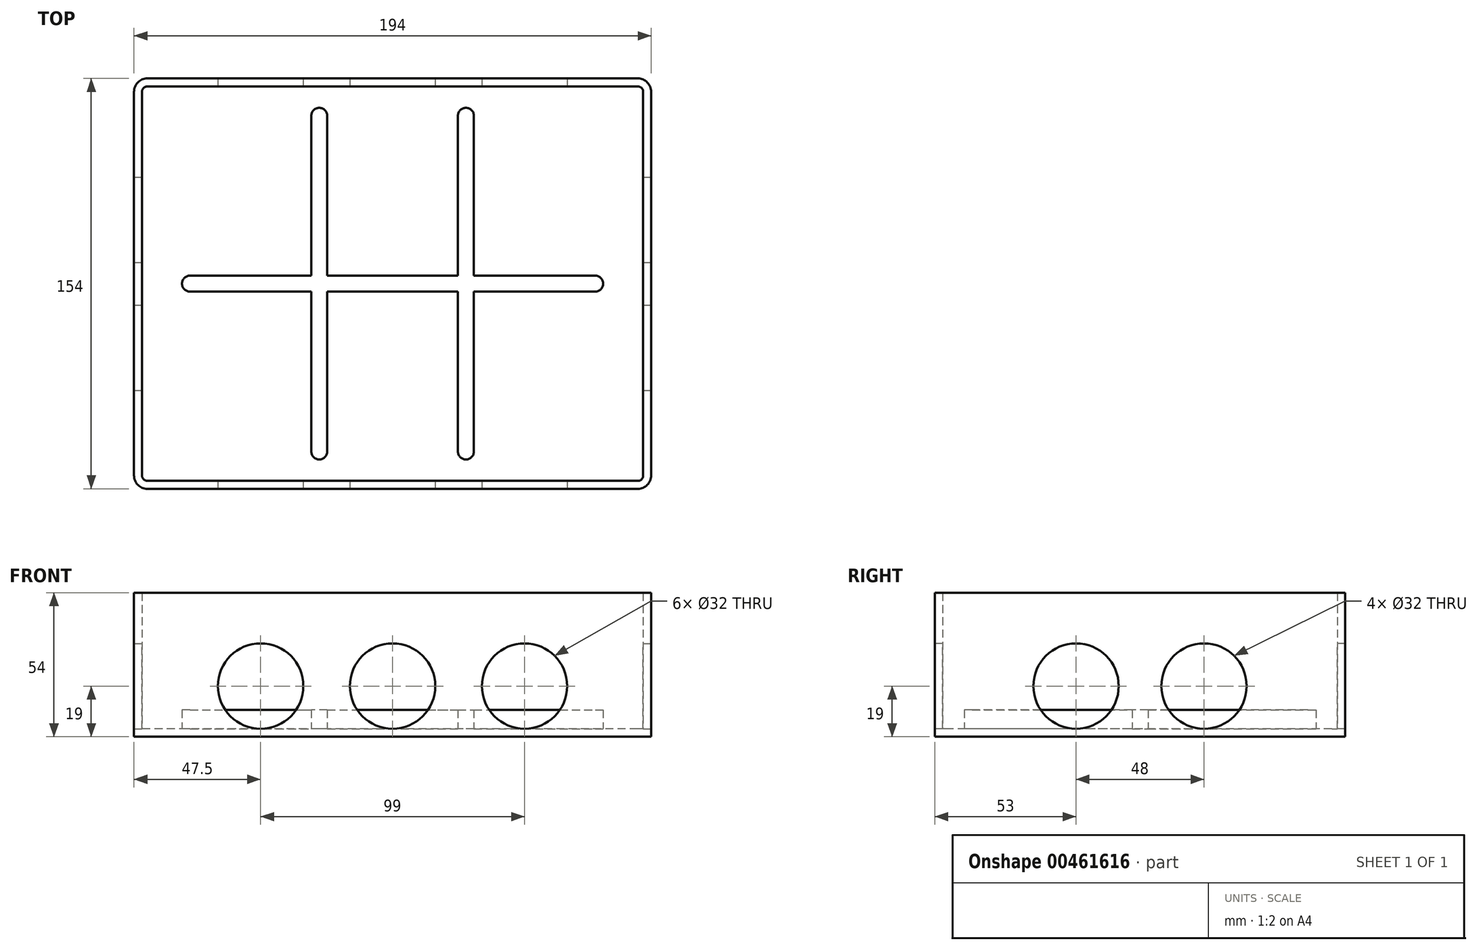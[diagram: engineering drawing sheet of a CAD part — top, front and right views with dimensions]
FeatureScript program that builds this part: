
annotation { "Feature Type Name" : "Feature", "Feature Type Description" : "" }
export const myFeature = defineFeature(function(context is Context, id is Id, definition is map)
    precondition{}
    {
        {
            var Q0;
            Q0=qCreatedBy(makeId("Top.planeOp"),FACE);
            var sketch = newSketch(context, id + "F0", { "sketchPlane" : qUnion([Q0])});
            skLineSegment(sketch, "E0.bottom", {"start": v(92, 77) * mm, "end": v(-92, 77) * mm});
            skLineSegment(sketch, "E0.top", {"start": v(92, -77) * mm, "end": v(-92, -77) * mm});
            skLineSegment(sketch, "E0.left", {"start": v(97, 72) * mm, "end": v(97, -72) * mm});
            skLineSegment(sketch, "E0.right", {"start": v(-97, 72) * mm, "end": v(-97, -72) * mm});
            skPoint(sketch, "E0.middle", {"position": v(0, 0) * mm});
            skPoint(sketch, "E1.visualSharp", {"position": v(-97, 77) * mm});
            skArc(sketch, "E1.filletArc", {"start": v(-92, 77) * mm, "mid": v(-95.54, 75.54) * mm, "end": v(-97, 72) * mm});
            skPoint(sketch, "E2.visualSharp", {"position": v(97, 77) * mm});
            skArc(sketch, "E2.filletArc", {"start": v(97, 72) * mm, "mid": v(95.54, 75.54) * mm, "end": v(92, 77) * mm});
            skPoint(sketch, "E3.visualSharp", {"position": v(97, -77) * mm});
            skArc(sketch, "E3.filletArc", {"start": v(92, -77) * mm, "mid": v(95.54, -75.54) * mm, "end": v(97, -72) * mm});
            skPoint(sketch, "E4.visualSharp", {"position": v(-97, -77) * mm});
            skArc(sketch, "E4.filletArc", {"start": v(-97, -72) * mm, "mid": v(-95.54, -75.54) * mm, "end": v(-92, -77) * mm});
            skSolve(sketch);
        }
        {
            var Q0;
            Q0=makeQuery(id+"F0.imprint","IMPRINT",FACE,{"disambiguationData":[TD([[makeQuery(id+"F0.imprint","IMPRINT",EDGE,{"derivedFrom":sQuery(id+"F0.wireOp",EDGE,"E0.bottom")}),1.0]])]});
            extrude(context, id + "F1", {"entities" : qUnion([Q0]), "depth" : 54 * mm});
        }
        {
            var Q0;
            Q0=makeQuery(id+"F1.opExtrude","CAP_FACE",FACE,{"disambiguationData":[OSD([sQuery(id+"F0.wireOp",EDGE,"E0.bottom"),sQuery(id+"F0.wireOp",EDGE,"E0.top"),sQuery(id+"F0.wireOp",EDGE,"E0.left"),sQuery(id+"F0.wireOp",EDGE,"E0.right"),sQuery(id+"F0.wireOp",EDGE,"E1.filletArc"),sQuery(id+"F0.wireOp",EDGE,"E2.filletArc"),sQuery(id+"F0.wireOp",EDGE,"E3.filletArc"),sQuery(id+"F0.wireOp",EDGE,"E4.filletArc")])],"isStart":false});
            shell(context, id + "F2", {"entities" : qUnion([Q0]), "thickness" : 3 * mm});
        }
        {
            var Q0;
            Q0=makeQuery(id+"F1.opExtrude","SWEPT_FACE",FACE,{"disambiguationData":[OSD([sQuery(id+"F0.wireOp",EDGE,"E0.top")])]});
            var sketch = newSketch(context, id + "F3", { "sketchPlane" : qUnion([Q0])});
            skCircle(sketch, "E5", {"center": v(0, 19) * mm, "radius": 16 * mm});
            skCircle(sketch, "E6", {"center": v(-49.5, 19) * mm, "radius": 16 * mm});
            skCircle(sketch, "E7", {"center": v(49.5, 19) * mm, "radius": 16 * mm});
            skSolve(sketch);
        }
        {
            var Q0;
            Q0=makeQuery(id+"F3.imprint","IMPRINT",FACE,{"disambiguationData":[TD([[makeQuery(id+"F3.imprint","IMPRINT",EDGE,{"derivedFrom":sQuery(id+"F3.wireOp",EDGE,"E6")}),1.0]])]});
            var Q1;
            Q1=makeQuery(id+"F3.imprint","IMPRINT",FACE,{"disambiguationData":[TD([[makeQuery(id+"F3.imprint","IMPRINT",EDGE,{"derivedFrom":sQuery(id+"F3.wireOp",EDGE,"E5")}),1.0]])]});
            var Q2;
            Q2=makeQuery(id+"F3.imprint","IMPRINT",FACE,{"disambiguationData":[TD([[makeQuery(id+"F3.imprint","IMPRINT",EDGE,{"derivedFrom":sQuery(id+"F3.wireOp",EDGE,"E7")}),1.0]])]});
            extrude(context, id + "F4", {"entities" : qUnion([Q0, Q1, Q2]), "operationType" : NewBodyOperationType.REMOVE, "endBound" : BoundingType.THROUGH_ALL, "oppositeDirection" : true, "depth" : 25 * mm});
        }
        {
            var Q0;
            Q0=makeQuery(id+"F1.opExtrude","SWEPT_FACE",FACE,{"disambiguationData":[OSD([sQuery(id+"F0.wireOp",EDGE,"E0.left")])]});
            var sketch = newSketch(context, id + "F5", { "sketchPlane" : qUnion([Q0])});
            skCircle(sketch, "E8", {"center": v(-24, 19) * mm, "radius": 16 * mm});
            skCircle(sketch, "E9", {"center": v(24, 19) * mm, "radius": 16 * mm});
            skSolve(sketch);
        }
        {
            var Q0;
            Q0=makeQuery(id+"F5.imprint","IMPRINT",FACE,{"disambiguationData":[TD([[makeQuery(id+"F5.imprint","IMPRINT",EDGE,{"derivedFrom":sQuery(id+"F5.wireOp",EDGE,"E8")}),1.0]])]});
            var Q1;
            Q1=makeQuery(id+"F5.imprint","IMPRINT",FACE,{"disambiguationData":[TD([[makeQuery(id+"F5.imprint","IMPRINT",EDGE,{"derivedFrom":sQuery(id+"F5.wireOp",EDGE,"E9")}),1.0]])]});
            extrude(context, id + "F6", {"entities" : qUnion([Q0, Q1]), "operationType" : NewBodyOperationType.REMOVE, "endBound" : BoundingType.THROUGH_ALL, "oppositeDirection" : true, "depth" : 25 * mm});
        }
        {
            var Q0;
            Q0=makeQuery(id+"F2.opShell","OFFSET_FACE",FACE,{"disambiguationData":[OSD([sQuery(id+"F0.wireOp",EDGE,"E0.bottom"),sQuery(id+"F0.wireOp",EDGE,"E0.top"),sQuery(id+"F0.wireOp",EDGE,"E0.left"),sQuery(id+"F0.wireOp",EDGE,"E0.right"),sQuery(id+"F0.wireOp",EDGE,"E1.filletArc"),sQuery(id+"F0.wireOp",EDGE,"E2.filletArc"),sQuery(id+"F0.wireOp",EDGE,"E3.filletArc"),sQuery(id+"F0.wireOp",EDGE,"E4.filletArc")])]});
            var sketch = newSketch(context, id + "F7", { "sketchPlane" : qUnion([Q0])});
            skCircle(sketch, "E10", {"center": v(-27.5, 62.98) * mm, "radius": 3 * mm});
            skCircle(sketch, "E11", {"center": v(27.5, 62.98) * mm, "radius": 3 * mm});
            skCircle(sketch, "E12", {"center": v(27.5, -62.98) * mm, "radius": 3 * mm});
            skCircle(sketch, "E13", {"center": v(-27.5, -62.98) * mm, "radius": 3 * mm});
            skCircle(sketch, "E14", {"center": v(-76, 0) * mm, "radius": 3 * mm});
            skCircle(sketch, "E15", {"center": v(76, 0) * mm, "radius": 3 * mm});
            skLineSegment(sketch, "E16", {"start": v(-30.5, -62.98) * mm, "end": v(-30.5, 62.98) * mm});
            skLineSegment(sketch, "E17", {"start": v(24.5, -62.98) * mm, "end": v(24.5, 62.98) * mm});
            skLineSegment(sketch, "E18", {"start": v(-76, -3) * mm, "end": v(76, -3) * mm});
            skLineSegment(sketch, "E19", {"start": v(-76, 3) * mm, "end": v(76, 3) * mm});
            skLineSegment(sketch, "E20", {"start": v(-24.5, 62.98) * mm, "end": v(-24.5, -62.98) * mm});
            skLineSegment(sketch, "E21", {"start": v(30.5, 62.98) * mm, "end": v(30.5, -62.98) * mm});
            skSolve(sketch);
        }
        {
            var Q0;
            Q0 = qSketchRegion(id + "F7", true);
            extrude(context, id + "F8", {"entities" : qUnion([Q0]), "operationType" : NewBodyOperationType.ADD, "depth" : 7 * mm});
        }
    });
